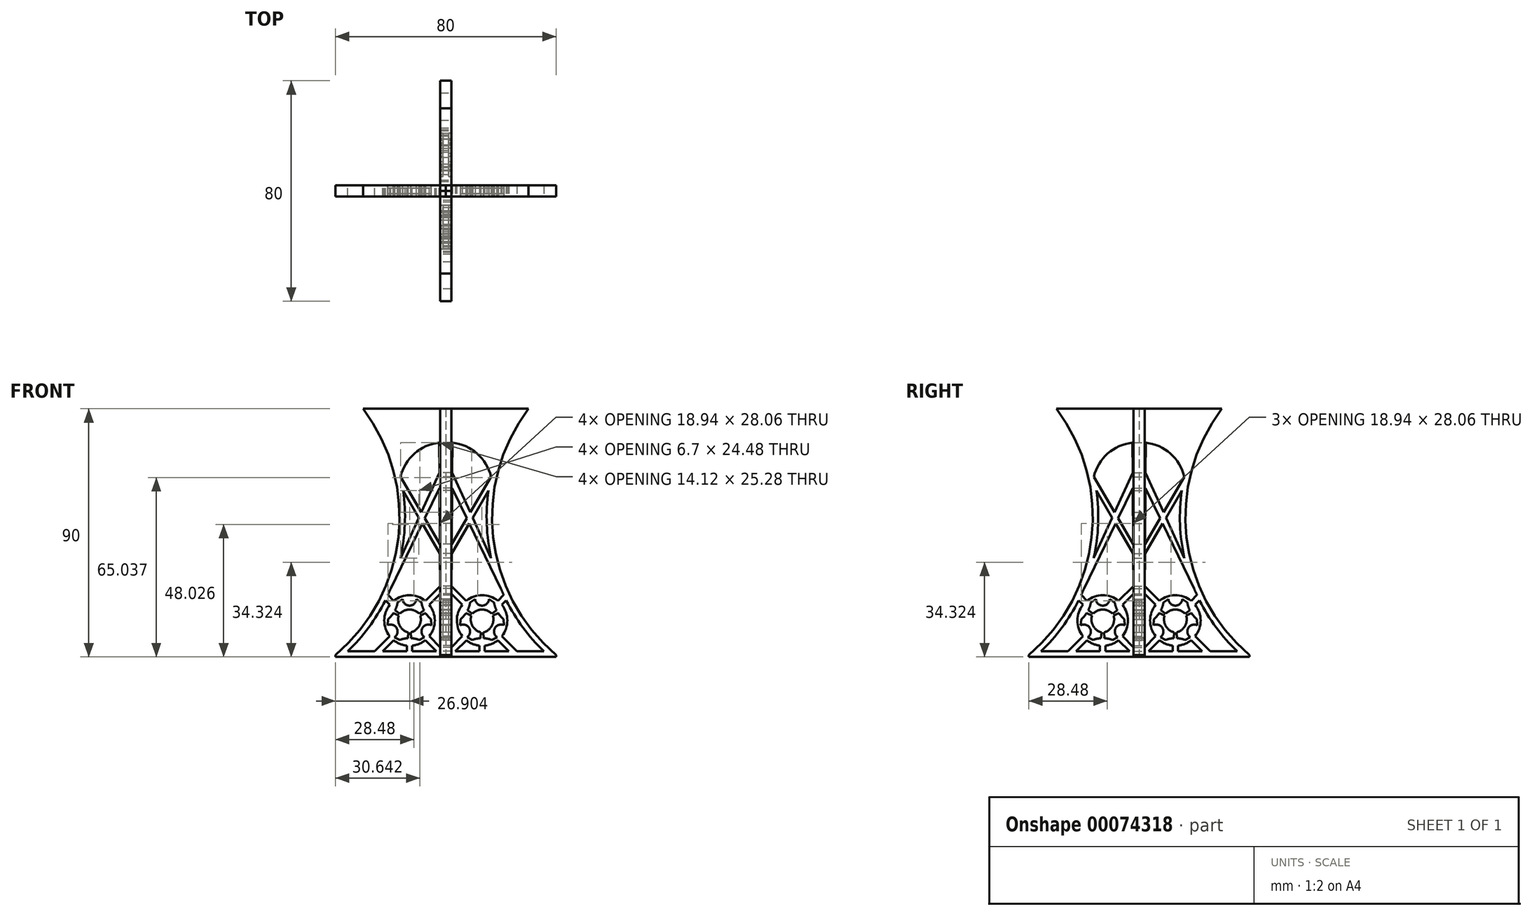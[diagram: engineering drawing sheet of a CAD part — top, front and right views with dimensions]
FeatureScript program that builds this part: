
annotation { "Feature Type Name" : "Feature", "Feature Type Description" : "" }
export const myFeature = defineFeature(function(context is Context, id is Id, definition is map)
    precondition{}
    {
        {
            var Q0;
            Q0=qCreatedBy(makeId("Right.planeOp"),FACE);
            var sketch = newSketch(context, id + "F0", { "sketchPlane" : qUnion([Q0])});
            skLineSegment(sketch, "E0", {"start": v(-30, 90) * mm, "end": v(0, 90) * mm});
            skLineSegment(sketch, "E1", {"start": v(0, 90) * mm, "end": v(0, 0) * mm});
            skLineSegment(sketch, "E2", {"start": v(0, 0) * mm, "end": v(-40, 0) * mm});
            skLineSegment(sketch, "E3", {"start": v(-40, 0) * mm, "end": v(-40, 0.68) * mm});
            skArc(sketch, "E4", {"start": v(-40, 0.68) * mm, "mid": v(-17.2, 43.35) * mm, "end": v(-30, 90) * mm});
            skArc(sketch, "E5", {"start": v(-6.02, 7.42) * mm, "mid": v(-4, 13.15) * mm, "end": v(-6.01, 18.88) * mm});
            skArc(sketch, "E6.0", {"start": v(-35.54, 2) * mm, "mid": v(-27.93, 10.66) * mm, "end": v(-21.9, 20.5) * mm});
            skLineSegment(sketch, "E6.1", {"start": v(-2, 2) * mm, "end": v(-12.16, 2) * mm});
            skLineSegment(sketch, "E7", {"start": v(-25.73, 2) * mm, "end": v(-20.3, 7.43) * mm});
            skLineSegment(sketch, "E8", {"start": v(-22.9, 2) * mm, "end": v(-18.89, 6.02) * mm});
            skLineSegment(sketch, "E9", {"start": v(-2, 3.4) * mm, "end": v(-6.02, 7.42) * mm});
            skLineSegment(sketch, "E10", {"start": v(-3.42, 2) * mm, "end": v(-7.43, 6.01) * mm});
            skLineSegment(sketch, "E11.trimOffspring", {"start": v(-7.42, 20.3) * mm, "end": v(-2.05, 25.66) * mm});
            skLineSegment(sketch, "E12.trimOffspring", {"start": v(-6.01, 18.88) * mm, "end": v(-2, 22.89) * mm});
            skLineSegment(sketch, "E13.trimOffspring", {"start": v(-18.88, 20.3) * mm, "end": v(-20.99, 22.4) * mm});
            skLineSegment(sketch, "E14.trimOffspring", {"start": v(-20.3, 18.89) * mm, "end": v(-21.9, 20.5) * mm});
            skArc(sketch, "E15.trimOffspring", {"start": v(-18.89, 6.02) * mm, "mid": v(-16.66, 4.7) * mm, "end": v(-14.16, 4.05) * mm});
            skArc(sketch, "E16.trimOffspring", {"start": v(-20.3, 18.89) * mm, "mid": v(-22.31, 13.16) * mm, "end": v(-20.3, 7.43) * mm});
            skArc(sketch, "E17.trimOffspring", {"start": v(-7.42, 20.3) * mm, "mid": v(-13.15, 22.31) * mm, "end": v(-18.88, 20.3) * mm});
            skLineSegment(sketch, "E18.trimOffspring", {"start": v(-2, 22.89) * mm, "end": v(-2, 2) * mm});
            skLineSegment(sketch, "E19", {"start": v(-14.16, 4.05) * mm, "end": v(-14.16, 2) * mm});
            skLineSegment(sketch, "E20", {"start": v(-12.16, 4.05) * mm, "end": v(-12.16, 2) * mm});
            skPoint(sketch, "E20.startSnap0", {"position": v(-14.16, 4.05) * mm});
            skArc(sketch, "E21.trimOffspring", {"start": v(-12.16, 4.05) * mm, "mid": v(-9.65, 4.7) * mm, "end": v(-7.43, 6.01) * mm});
            skLineSegment(sketch, "E22.trimOffspring", {"start": v(-14.16, 2) * mm, "end": v(-35.54, 2) * mm});
            skLineSegment(sketch, "E23", {"start": v(-25.35, 13.16) * mm, "end": v(3.04, 13.16) * mm, "construction": true});
            skLineSegment(sketch, "E24", {"start": v(-13.16, 13.16) * mm, "end": v(-0.47, 22.2) * mm, "construction": true});
            skLineSegment(sketch, "E25", {"start": v(-13.16, 13.16) * mm, "end": v(-2.45, 29.33) * mm, "construction": true});
            skLineSegment(sketch, "E26", {"start": v(-13.16, 13.16) * mm, "end": v(-8.24, 28.3) * mm, "construction": true});
            skLineSegment(sketch, "E27", {"start": v(-9.65, 15.66) * mm, "end": v(-7.9, 16.9) * mm});
            skLineSegment(sketch, "E28", {"start": v(-10.64, 20.91) * mm, "end": v(-8.82, 19.7) * mm});
            skArc(sketch, "E29", {"start": v(-8.82, 19.7) * mm, "mid": v(-8.49, 18.27) * mm, "end": v(-7.9, 16.9) * mm});
            skLineSegment(sketch, "E30", {"start": v(-13.16, 13.16) * mm, "end": v(-18.41, 16.9) * mm, "construction": true});
            skLineSegment(sketch, "E31", {"start": v(-13.16, 13.16) * mm, "end": v(-18.55, 21.3) * mm, "construction": true});
            skLineSegment(sketch, "E32", {"start": v(-13.16, 13.16) * mm, "end": v(-16.83, 24.47) * mm, "construction": true});
            skLineSegment(sketch, "E33", {"start": v(-16.66, 15.66) * mm, "end": v(-18.41, 16.9) * mm});
            skLineSegment(sketch, "E34", {"start": v(-15.68, 20.91) * mm, "end": v(-17.5, 19.7) * mm});
            skArc(sketch, "E35", {"start": v(-15.68, 20.91) * mm, "mid": v(-13.16, 18.56) * mm, "end": v(-10.64, 20.91) * mm});
            skArc(sketch, "E36", {"start": v(-18.41, 16.9) * mm, "mid": v(-17.83, 18.27) * mm, "end": v(-17.5, 19.7) * mm});
            skArc(sketch, "E37", {"start": v(-9.65, 15.66) * mm, "mid": v(-13.16, 17.16) * mm, "end": v(-16.66, 15.66) * mm});
            skLineSegment(sketch, "E38", {"start": v(-25.53, 20.8) * mm, "end": v(-2.82, 20.8) * mm, "construction": true});
            skLineSegment(sketch, "E39", {"start": v(-16.66, 15.66) * mm, "end": v(-2.86, 15.66) * mm, "construction": true});
            skArc(sketch, "E40.1.0", {"start": v(-18.61, 7.1) * mm, "mid": v(-17.84, 10.45) * mm, "end": v(-21.13, 11.46) * mm});
            skLineSegment(sketch, "E40.1.1", {"start": v(-18.61, 7.1) * mm, "end": v(-16.66, 6.12) * mm});
            skArc(sketch, "E40.1.2", {"start": v(-13.77, 6.72) * mm, "mid": v(-15.25, 6.56) * mm, "end": v(-16.66, 6.12) * mm});
            skLineSegment(sketch, "E40.1.3", {"start": v(-13.57, 8.86) * mm, "end": v(-13.77, 6.72) * mm});
            skArc(sketch, "E40.1.4", {"start": v(-17.08, 14.94) * mm, "mid": v(-16.62, 11.15) * mm, "end": v(-13.57, 8.86) * mm});
            skLineSegment(sketch, "E40.1.5", {"start": v(-17.08, 14.94) * mm, "end": v(-19.03, 15.83) * mm});
            skArc(sketch, "E40.1.6", {"start": v(-21, 13.64) * mm, "mid": v(-19.92, 14.64) * mm, "end": v(-19.03, 15.83) * mm});
            skLineSegment(sketch, "E40.1.7", {"start": v(-21.13, 11.46) * mm, "end": v(-21, 13.64) * mm});
            skArc(sketch, "E40.2.0", {"start": v(-5.18, 11.46) * mm, "mid": v(-8.47, 10.45) * mm, "end": v(-7.7, 7.1) * mm});
            skLineSegment(sketch, "E40.2.1", {"start": v(-5.18, 11.46) * mm, "end": v(-5.31, 13.64) * mm});
            skArc(sketch, "E40.2.2", {"start": v(-7.28, 15.83) * mm, "mid": v(-6.4, 14.64) * mm, "end": v(-5.31, 13.64) * mm});
            skLineSegment(sketch, "E40.2.3", {"start": v(-9.23, 14.94) * mm, "end": v(-7.28, 15.83) * mm});
            skArc(sketch, "E40.2.4", {"start": v(-12.74, 8.86) * mm, "mid": v(-9.7, 11.15) * mm, "end": v(-9.23, 14.94) * mm});
            skLineSegment(sketch, "E40.2.5", {"start": v(-12.74, 8.86) * mm, "end": v(-12.54, 6.72) * mm});
            skArc(sketch, "E40.2.6", {"start": v(-9.65, 6.12) * mm, "mid": v(-11.06, 6.56) * mm, "end": v(-12.54, 6.72) * mm});
            skLineSegment(sketch, "E40.2.7", {"start": v(-7.7, 7.1) * mm, "end": v(-9.65, 6.12) * mm});
            skLineSegment(sketch, "E41", {"start": v(-2.37, 77.68) * mm, "end": v(-2.14, 40.93) * mm});
            skArc(sketch, "E42.trimOffspring", {"start": v(-35.54, 2) * mm, "mid": v(-26.56, 12.58) * mm, "end": v(-19.95, 24.78) * mm});
            skLineSegment(sketch, "E43", {"start": v(-16.45, 35.79) * mm, "end": v(-9.74, 50.45) * mm});
            skLineSegment(sketch, "E44", {"start": v(-2.27, 61.23) * mm, "end": v(-7.6, 50.24) * mm});
            skLineSegment(sketch, "E45", {"start": v(-16.42, 65.3) * mm, "end": v(-8.86, 52.4) * mm});
            skLineSegment(sketch, "E46", {"start": v(-2.12, 37.44) * mm, "end": v(-8.51, 48.35) * mm});
            skLineSegment(sketch, "E47.trimOffspring", {"start": v(-8.86, 52.4) * mm, "end": v(-2.3, 66.74) * mm});
            skLineSegment(sketch, "E48.trimOffspring", {"start": v(-9.74, 50.45) * mm, "end": v(-15.49, 60.26) * mm});
            skLineSegment(sketch, "E49.trimOffspring", {"start": v(-7.6, 50.24) * mm, "end": v(-2.14, 40.93) * mm});
            skLineSegment(sketch, "E50.trimOffspring", {"start": v(-2.12, 37.44) * mm, "end": v(-2.05, 25.66) * mm});
            skArc(sketch, "E51.trimOffspring", {"start": v(-16.45, 35.79) * mm, "mid": v(-14.85, 47.98) * mm, "end": v(-15.49, 60.26) * mm});
            skLineSegment(sketch, "E52.trimOffspring", {"start": v(-8.51, 48.35) * mm, "end": v(-19.95, 24.78) * mm});
            skArc(sketch, "E53", {"start": v(-2.37, 77.68) * mm, "mid": v(-11.36, 73.73) * mm, "end": v(-16.42, 65.3) * mm});
            skSolve(sketch);
        }
        {
            var Q0;
            Q0=qSketchRegion(id+"F0",true);
            extrude(context, id + "F1", {"entities" : qUnion([Q0]), "depth" : 2 * mm, "hasSecondDirection" : true, "secondDirectionOppositeDirection" : true, "secondDirectionDepth" : 2 * mm});
        }
        {
            var Q0;
            Q0=qCreatedBy(makeId("Right.planeOp"),FACE);
            var sketch = newSketch(context, id + "F2", { "sketchPlane" : qUnion([Q0])});
            skLineSegment(sketch, "E54", {"start": v(0, 81) * mm, "end": v(0, -28.5) * mm, "construction": true});
            skSolve(sketch);
        }
        {
            var Q0;
            Q0=makeQuery(id+"F1.opExtrude","SWEPT_BODY",BODY,{"disambiguationData":[OSD([sQuery(id+"F0.wireOp",EDGE,"E0"),sQuery(id+"F0.wireOp",EDGE,"E1"),sQuery(id+"F0.wireOp",EDGE,"N8EfN9Iy-VFxy-i62X-S3Tn-et34u0hB6ofw"),sQuery(id+"F0.wireOp",EDGE,"ofOerVMI-8AtS-AqWo-Xm8z-ZVAlB3EUovam"),sQuery(id+"F0.wireOp",EDGE,"ba3e6201-bb00-4176-be12-0bcf97df4df2"),sQuery(id+"F0.wireOp",EDGE,"k6Ju8hmT-RXya-gFIe-6RDm-fDKX84Fwp2G4"),sQuery(id+"F0.wireOp",EDGE,"dTDJtstR-zKxY-rc8w-sIGn-4ASnDpw26A23"),sQuery(id+"F0.wireOp",EDGE,"Cvr0LfUC-tO0D-IxcI-B5Ti-WW2sAGeSHFF8"),sQuery(id+"F0.wireOp",EDGE,"DwRJblST-1CEV-pcTT-NFQT-YytcCcE5cTGx"),sQuery(id+"F0.wireOp",EDGE,"973229ff-babc-457a-ac66-6eeaf75bea45")])]});
            var Q1;
            Q1=sQuery(id+"F2.wireOp",EDGE,"E54");
            circularPattern(context, id + "F3", {"entities" : qUnion([Q0]), "axis" : qUnion([Q1]), "angle" : 90 * degree, "instanceCount" : round(4)});
        }
        {
            var Q0;
            Q0=qCreatedBy(makeId("Right.planeOp"),FACE);
            var sketch = newSketch(context, id + "F4", { "sketchPlane" : qUnion([Q0])});
            skCircle(sketch, "E55", {"center": v(13.16, 13.16) * mm, "radius": 8.72 * mm});
            skLineSegment(sketch, "E56", {"start": v(0, -9.43) * mm, "end": v(0, 24.64) * mm, "construction": true});
            skSolve(sketch);
        }
        {
            var Q0;
            Q0=qCreatedBy(makeId("Right.planeOp"),FACE);
            var sketch = newSketch(context, id + "F5", { "sketchPlane" : qUnion([Q0])});
            skLineSegment(sketch, "E57", {"start": v(0, 7.6) * mm, "end": v(0, -25.74) * mm, "construction": true});
            skSolve(sketch);
        }
        {
            var Q0;
            Q0=qSketchRegion(id+"F4",true);
            extrude(context, id + "F6", {"entities" : qUnion([Q0]), "operationType" : NewBodyOperationType.ADD, "depth" : 1 * mm, "hasSecondDirection" : true, "secondDirectionOppositeDirection" : true, "secondDirectionDepth" : 1 * mm});
        }
        {
            var Q0;
            Q0=makeQuery(id+"F3.opPattern","COPY",BODY,{"derivedFrom":makeQuery(id+"F1.opExtrude","SWEPT_BODY",BODY,{"disambiguationData":[OSD([sQuery(id+"F0.wireOp",EDGE,"E0"),sQuery(id+"F0.wireOp",EDGE,"E1"),sQuery(id+"F0.wireOp",EDGE,"E2"),sQuery(id+"F0.wireOp",EDGE,"E3"),sQuery(id+"F0.wireOp",EDGE,"E4"),sQuery(id+"F0.wireOp",EDGE,"E5"),sQuery(id+"F0.wireOp",EDGE,"E6.0"),sQuery(id+"F0.wireOp",EDGE,"E6.1"),sQuery(id+"F0.wireOp",EDGE,"E6.2"),sQuery(id+"F0.wireOp",EDGE,"E6.3"),sQuery(id+"F0.wireOp",EDGE,"E7"),sQuery(id+"F0.wireOp",EDGE,"E8"),sQuery(id+"F0.wireOp",EDGE,"E9"),sQuery(id+"F0.wireOp",EDGE,"E10"),sQuery(id+"F0.wireOp",EDGE,"E11.trimOffspring"),sQuery(id+"F0.wireOp",EDGE,"E12.trimOffspring"),sQuery(id+"F0.wireOp",EDGE,"E13.trimOffspring"),sQuery(id+"F0.wireOp",EDGE,"E14.trimOffspring"),sQuery(id+"F0.wireOp",EDGE,"E15.trimOffspring"),sQuery(id+"F0.wireOp",EDGE,"E16.trimOffspring"),sQuery(id+"F0.wireOp",EDGE,"f6aabd91-0355-4ce8-b6d2-6d85713953a7.trimOffspring"),sQuery(id+"F0.wireOp",EDGE,"E17.trimOffspring"),sQuery(id+"F0.wireOp",EDGE,"E18.trimOffspring"),sQuery(id+"F0.wireOp",EDGE,"E19"),sQuery(id+"F0.wireOp",EDGE,"E20"),sQuery(id+"F0.wireOp",EDGE,"E21.trimOffspring"),sQuery(id+"F0.wireOp",EDGE,"E22.trimOffspring"),sQuery(id+"F0.wireOp",EDGE,"E27"),sQuery(id+"F0.wireOp",EDGE,"E28"),sQuery(id+"F0.wireOp",EDGE,"E29"),sQuery(id+"F0.wireOp",EDGE,"E33"),sQuery(id+"F0.wireOp",EDGE,"E34"),sQuery(id+"F0.wireOp",EDGE,"E35"),sQuery(id+"F0.wireOp",EDGE,"E36"),sQuery(id+"F0.wireOp",EDGE,"E37"),sQuery(id+"F0.wireOp",EDGE,"E40.1.0"),sQuery(id+"F0.wireOp",EDGE,"E40.1.1"),sQuery(id+"F0.wireOp",EDGE,"E40.1.2"),sQuery(id+"F0.wireOp",EDGE,"E40.1.3"),sQuery(id+"F0.wireOp",EDGE,"E40.1.4"),sQuery(id+"F0.wireOp",EDGE,"E40.1.5"),sQuery(id+"F0.wireOp",EDGE,"E40.1.6"),sQuery(id+"F0.wireOp",EDGE,"E40.1.7"),sQuery(id+"F0.wireOp",EDGE,"E40.2.0"),sQuery(id+"F0.wireOp",EDGE,"E40.2.1"),sQuery(id+"F0.wireOp",EDGE,"E40.2.2"),sQuery(id+"F0.wireOp",EDGE,"E40.2.3"),sQuery(id+"F0.wireOp",EDGE,"E40.2.4"),sQuery(id+"F0.wireOp",EDGE,"E40.2.5"),sQuery(id+"F0.wireOp",EDGE,"E40.2.6"),sQuery(id+"F0.wireOp",EDGE,"E40.2.7")])]}),"instanceName":"2"});
            var Q1;
            Q1=sQuery(id+"F5.wireOp",EDGE,"E57");
            circularPattern(context, id + "F7", {"entities" : qUnion([Q0]), "axis" : qUnion([Q1]), "angle" : 90 * degree, "instanceCount" : round(4)});
        }
    });
